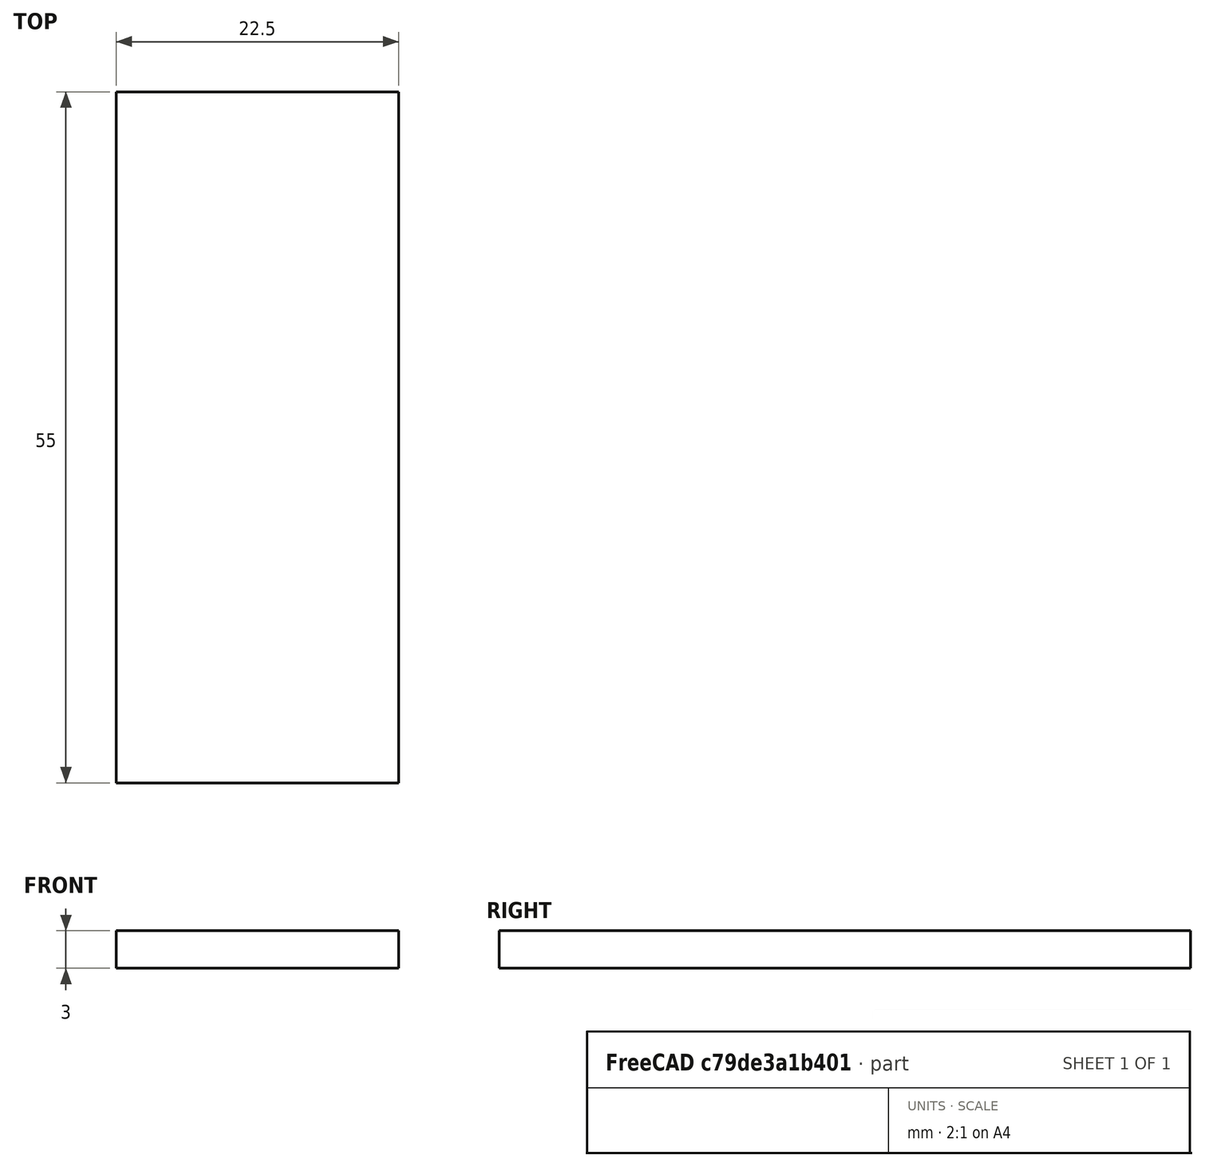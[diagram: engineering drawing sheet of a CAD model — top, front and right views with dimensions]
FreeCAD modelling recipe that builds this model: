
FCSTD DOCUMENT  (FreeCAD 2024.409R14555 (Git shallow))
Label: multi-sensor-isolator
License: All rights reserved
LicenseURL: https://en.wikipedia.org/wiki/All_rights_reserved
objects: Sketcher::SketchObject×1, PartDesign::Pad×1, PartDesign::Body×1
note: 6 computed .brp shape members not serialized (recipe doc carries the construction recipe); baked Part::Feature solids carry a one-line shape summary decoded from their .brp

FEATURE [Sketcher::SketchObject] Sketch
  ArcFitTolerance = 1e-06
  AttachmentSupport = -> [XY_Plane]
  ExternalBSplineMaxDegree = 5
  ExternalBSplineTolerance = 0.0001
  FullyConstrained = true
  InternalTolerance = 1e-06
  InvalidShape = false
  MakeInternals = false
  MapMode = 5
  Support = -> [XY_Plane]
  TreeRank = 11
  ValidateShape = false
  sketch-geometry (5):
    g0: LineSegment StartX=-11.25 StartY=27.5 StartZ=0 EndX=-11.25 EndY=-27.5 EndZ=0
    g1: LineSegment StartX=-11.25 StartY=-27.5 StartZ=0 EndX=11.25 EndY=-27.5 EndZ=0
    g2: LineSegment StartX=11.25 StartY=-27.5 StartZ=0 EndX=11.25 EndY=27.5 EndZ=0
    g3: LineSegment StartX=11.25 StartY=27.5 StartZ=0 EndX=-11.25 EndY=27.5 EndZ=0
    g4: GeomPoint [constr] X=0 Y=0 Z=0
  constraints (12):
    c: Coincident(g0,g1)
    c: Coincident(g1,g2)
    c: Coincident(g2,g3)
    c: Coincident(g3,g0)
    c: Horizontal(g1)
    c: Horizontal(g3)
    c: Vertical(g0)
    c: Vertical(g2)
    c: Symmetric(g1,g0,g4)
    c: Coincident(g4,g-1)
    c: DistanceX(g3,g3) = 22.5
    c: DistanceY(g2,g2) = 55
FEATURE [PartDesign::Pad] Pad
  AddSubType = 0
  AlongSketchNormal = false
  AutoTaperInnerAngle = true
  CheckUpToFaceLimits = true
  ClaimChildren = false
  Direction = (0,0,1)
  Fit = 0
  FitJoin = 0
  InnerFit = 0
  InnerFitJoin = 0
  InvalidShape = false
  Length = 3
  Length2 = 10
  Linearize = true
  NewSolid = false
  Profile = -> Sketch
  ReferenceAxis = -> Sketch [N_Axis]
  Suppress = false
  TaperInnerAngle = 0
  TaperInnerAngleRev = 0
  TreeRank = 12
  Type = 0
  ValidateShape = false
  _ProfileBasedVersion = 1
FEATURE [PartDesign::Body] Body
  AutoGroupSolids = false
  ClaimAllChildren = false
  ExportMode = 0
  Group = -> [Sketch,Pad]
  InvalidShape = false
  Origin = -> Origin
  Tip = -> Pad
  TreeRank = 10
  ValidateShape = false
  _ExportChildren = -> [Pad]
  _GroupVersion = 1
